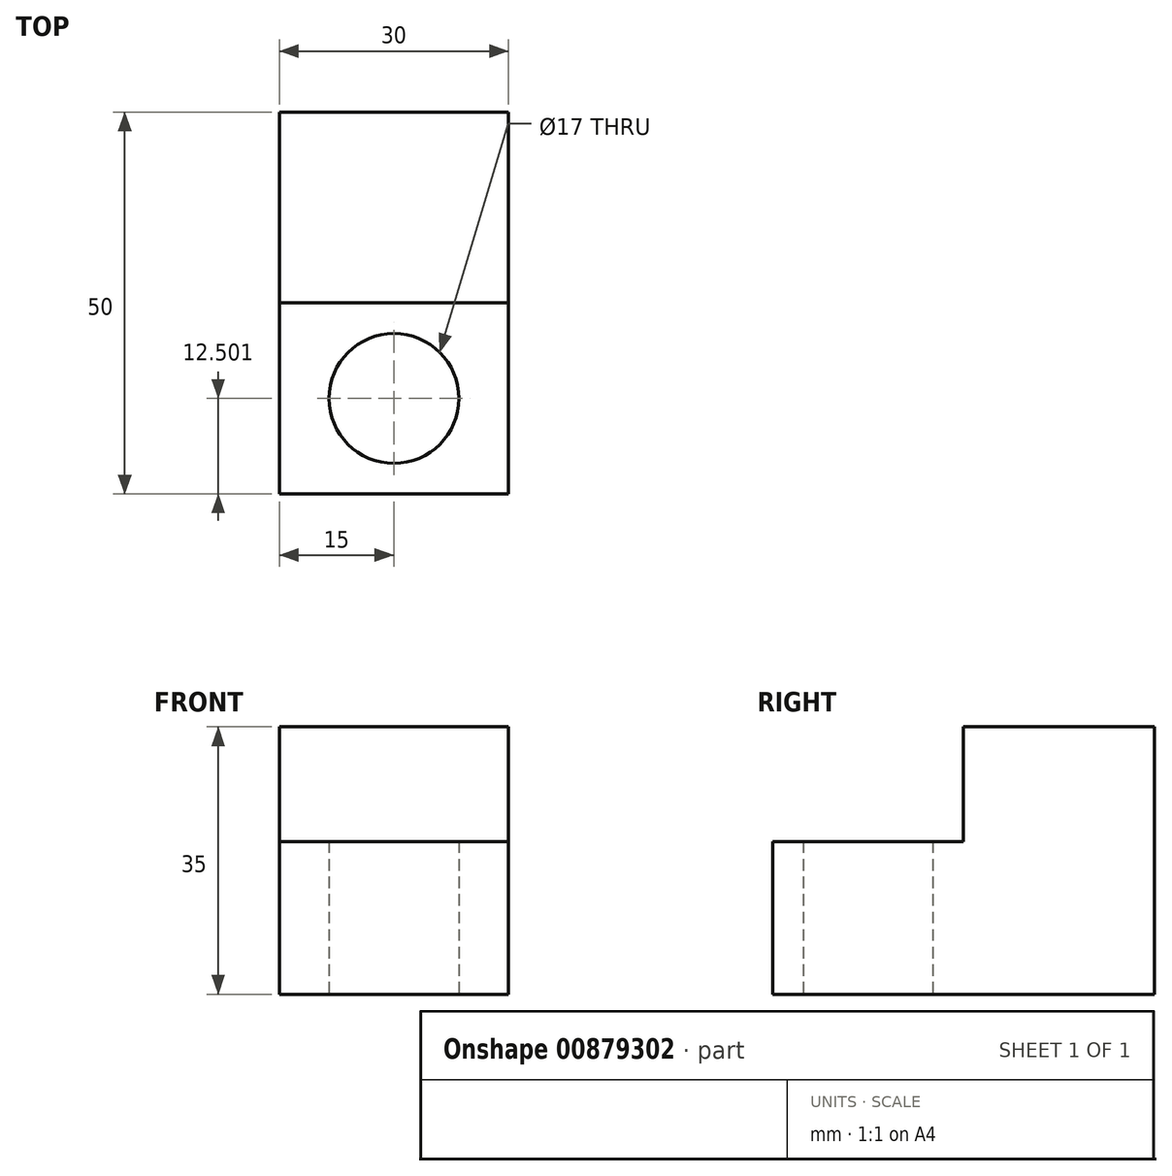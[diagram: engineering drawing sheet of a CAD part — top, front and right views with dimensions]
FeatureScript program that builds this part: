
annotation { "Feature Type Name" : "Feature", "Feature Type Description" : "" }
export const myFeature = defineFeature(function(context is Context, id is Id, definition is map)
    precondition{}
    {
        {
            var Q0;
            Q0=qCreatedBy(makeId("Right.planeOp"),FACE);
            var sketch = newSketch(context, id + "F0", { "sketchPlane" : qUnion([Q0])});
            skLineSegment(sketch, "E0", {"start": v(46.75, 50.6) * mm, "end": v(46.75, 15.6) * mm});
            skLineSegment(sketch, "E1", {"start": v(46.75, 15.6) * mm, "end": v(-3.25, 15.6) * mm});
            skLineSegment(sketch, "E2", {"start": v(-3.25, 15.6) * mm, "end": v(-3.25, 35.6) * mm});
            skLineSegment(sketch, "E3", {"start": v(46.75, 50.6) * mm, "end": v(21.75, 50.6) * mm});
            skLineSegment(sketch, "E4", {"start": v(-3.25, 35.6) * mm, "end": v(21.75, 35.6) * mm});
            skLineSegment(sketch, "E5", {"start": v(21.75, 50.6) * mm, "end": v(21.75, 35.6) * mm});
            skSolve(sketch);
        }
        {
            var Q0;
            Q0=makeQuery(id+"F0.imprint","IMPRINT",FACE,{"disambiguationData":[TD([[makeQuery(id+"F0.imprint","IMPRINT",EDGE,{"derivedFrom":sQuery(id+"F0.wireOp",EDGE,"E0")}),-1.0]])]});
            extrude(context, id + "F1", {"entities" : qUnion([Q0]), "depth" : 30 * mm, "offsetDistance" : 25 * mm});
        }
        {
            var Q0;
            Q0=qCreatedBy(makeId("Top.planeOp"),FACE);
            var sketch = newSketch(context, id + "F2", { "sketchPlane" : qUnion([Q0])});
            skCircle(sketch, "E6", {"center": v(15, 9.25) * mm, "radius": 8.5 * mm});
            skSolve(sketch);
        }
        {
            var Q0;
            Q0=sQuery(id+"F2.wireOp",VERTEX,"E6.center");
            var Q1;
            Q1=makeQuery(id+"F1.opExtrude","SWEPT_BODY",BODY,{"disambiguationData":[OSD([sQuery(id+"F0.wireOp",EDGE,"E0"),sQuery(id+"F0.wireOp",EDGE,"E1"),sQuery(id+"F0.wireOp",EDGE,"E2"),sQuery(id+"F0.wireOp",EDGE,"E3"),sQuery(id+"F0.wireOp",EDGE,"E4"),sQuery(id+"F0.wireOp",EDGE,"E5")])]});
            hole(context, id + "F3", {"style" : HoleStyle.SIMPLE, "endStyle" : HoleEndStyle.THROUGH, "oppositeDirection" : true, "holeDiameter" : 17 * mm, "majorDiameter" : 5 * mm, "isTappedThrough" : true, "tappedDepth" : 12 * mm, "tapClearance" : 3, "locations" : qUnion([Q0]), "scope" : qUnion([Q1])});
        }
    });
